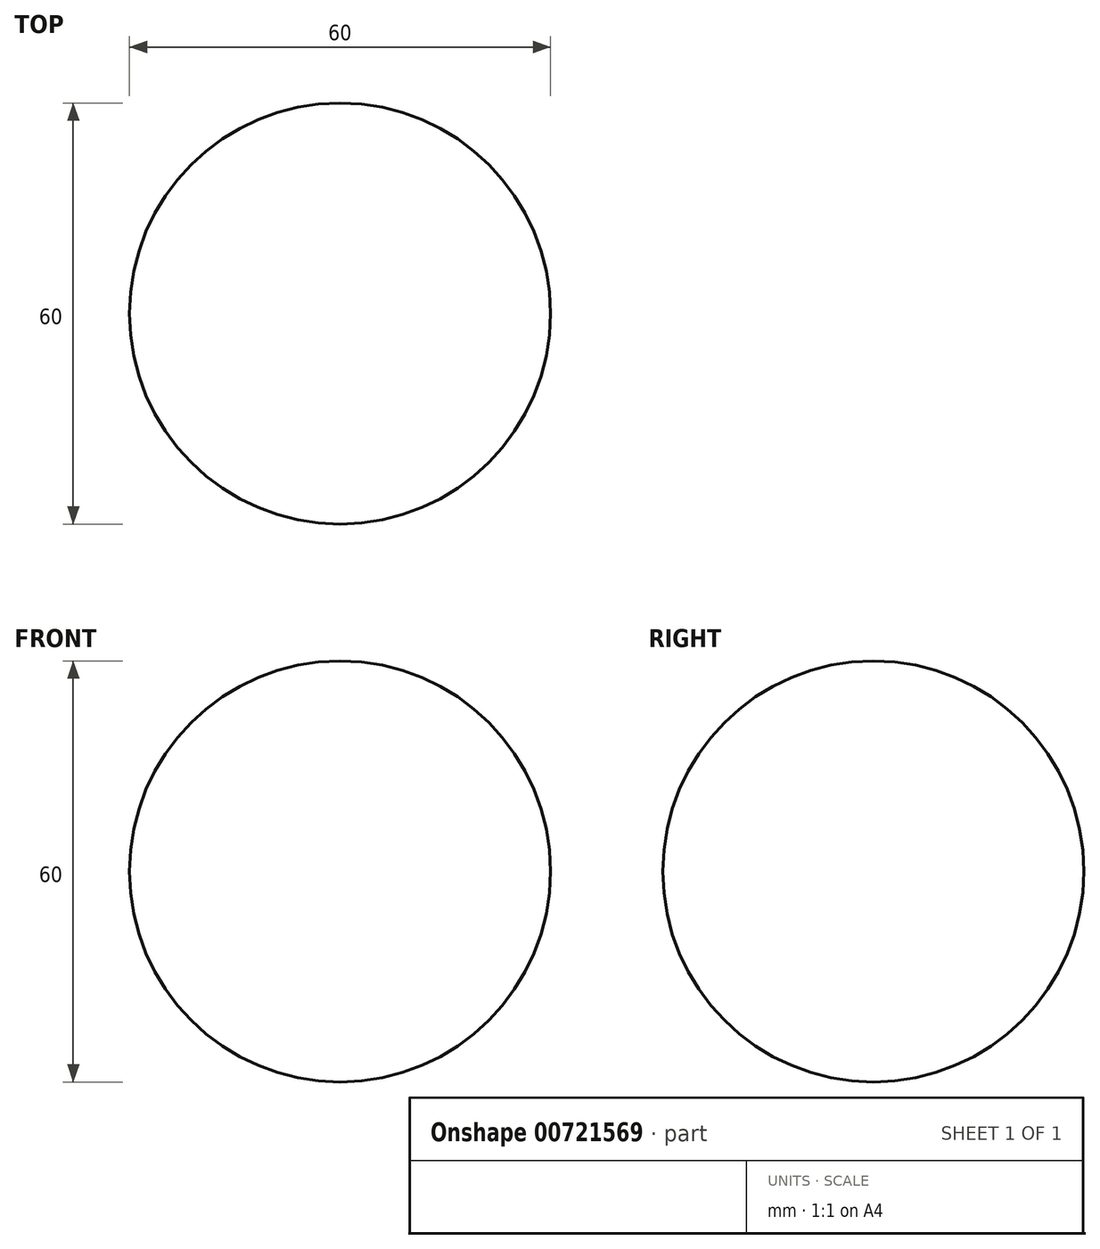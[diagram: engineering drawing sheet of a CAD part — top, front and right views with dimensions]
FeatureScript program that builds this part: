
annotation { "Feature Type Name" : "Feature", "Feature Type Description" : "" }
export const myFeature = defineFeature(function(context is Context, id is Id, definition is map)
    precondition{}
    {
        {
            var Q0;
            Q0=qCreatedBy(makeId("Top.planeOp"),FACE);
            var sketch = newSketch(context, id + "F0", { "sketchPlane" : qUnion([Q0])});
            skCircle(sketch, "E0", {"center": v(0, 0) * mm, "radius": 30 * mm});
            skSolve(sketch);
        }
        {
            var Q0;
            Q0 = qSketchRegion(id + "F0", true);
            extrude(context, id + "F1", {"entities" : qUnion([Q0]), "depth" : 60 * mm, "offsetDistance" : 25 * mm});
        }
        {
            var Q0;
            Q0=makeQuery(id+"F1.opExtrude","CAP_FACE",FACE,{"disambiguationData":[OSD([sQuery(id+"F0.wireOp",EDGE,"E0")])],"isStart":true});
            var Q1;
            Q1=makeQuery(id+"F1.opExtrude","CAP_FACE",FACE,{"disambiguationData":[OSD([sQuery(id+"F0.wireOp",EDGE,"E0")])],"isStart":false});
            fillet(context, id + "F2", {"entities" : qUnion([Q0, Q1]), "radius" : 30 * mm, "tangentPropagation" : true, "allowEdgeOverflow" : false});
        }
    });
